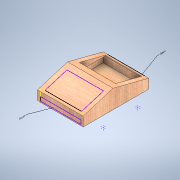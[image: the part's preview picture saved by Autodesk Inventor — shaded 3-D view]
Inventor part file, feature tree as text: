
AUTODESK INVENTOR PART (.ipt)
format: ipt  version: 2020 (Build 240168000, 168)  size: 160,256 bytes
history: native  units: in
note: dims shown in document units (in); Inventor stores cm internally (conversion verified against a paired STEP export)
features: sketch x7, other x3, extrude x3, shell x1
ambient origin geometry x8: Origin, YZ Plane, XZ Plane, XY Plane, X Axis, Y Axis, Z Axis, Center Point
bodies: Solid1 (feature_tree)
feature tree (14):
  other  "Annotations"
  extrude  "Extrusion1"  Depth=14.1732in
  shell  "Shell1"  Thickness=2.0472in
  sketch  "3D Sketch5"
  extrude  "Extrusion4"  Depth=0.5906in
  extrude  "Extrusion5"  Depth=0.9843in
  sketch  "Sketch10"  dims[d31=0.9843in]
  sketch  "Sketch11"  dims[d32=1.1811in d33=0.0in]
  sketch  "Sketch12"  dims[d5=0.1354in d6=0.0742in d7=0.0893in d8=0.1577in]
  sketch  "Sketch1"  dims[d0=9.8425in d1=14.1732in d2=2.0472in d3=0.0in]
  sketch  "Sketch8"  dims[d4=0.5906in d27=0.1168in]
  sketch  "Sketch9"  dims[d28=0.3937in d29=0.0in d30=0.9843in]
  other  "Leader Text 1"
  other  "Leader Text 2"
